# Revit family: FP_Revit_18_HPB4819-12_N_Rangehood_90000973B
name_source: partatom
category: Specialty Equipment
revit_build: Autodesk Revit 2018 (Build: 20170223_1515(x64)
units: mm (PartAtom-declared; Revit-internal decimal feet)

## family parameters
Always vertical = Yes
Cut with Voids When Loaded = Yes
OmniClass Number = 23.40.40.00
OmniClass Title = Food Service Equipment and Furnishings
Part Type = Normal
Room Calculation Point = No
Round Connector Dimension = Use Diameter
Shared = No
Work Plane-Based = No

## types (1)
- FP_Revit_18_HPB4819-12_N_Rangehood_90000973B
    Cavity - Depth = 455 mm
    Cavity - Height = 435 mm  [stored 1.42717 ft]
    Cavity - Width = 1155 mm  [stored 3.78937 ft]
    Chassis - Depth = 452 mm  [stored 1.48294 ft]
    Chassis - Height = 380 mm
    Chassis - Width = 1150 mm  [stored 3.77297 ft]
    Connector Description - Electrical = 120 V, 15 A, Fused electrical supply
    Connector Description - Extraction = 250mm (9 3/16") Outside diameter of ducting outlet, 1100 CFM
    Description = 48" Integrated Insert Rangehood
    Manufacturer = Fisher & Paykel Appliances
    Material - Body = Fisher & Paykel - Stainless Steel
    Material - Glass = Fisher & Paykel - White Bezel
    Model = HPB4819-12_N
    Product - Depth = 480 mm  [stored 1.5748 ft]
    Product - Height = 462 mm  [stored 1.51575 ft]
    Product - Width = 1180 mm  [stored 3.87139 ft]
    URL = www.fisherpaykel.com
    Visibility - Clearance Required = Yes
    Visibility - Duct Adaptor = Yes

note: [stored X ft] marks values corroborated as IEEE doubles in the binary element streams (Revit-internal decimal feet)

## geometry (parser evidence)
native form markers: Blend x2, Sweep x6
no freeform markers — native parametric forms only
